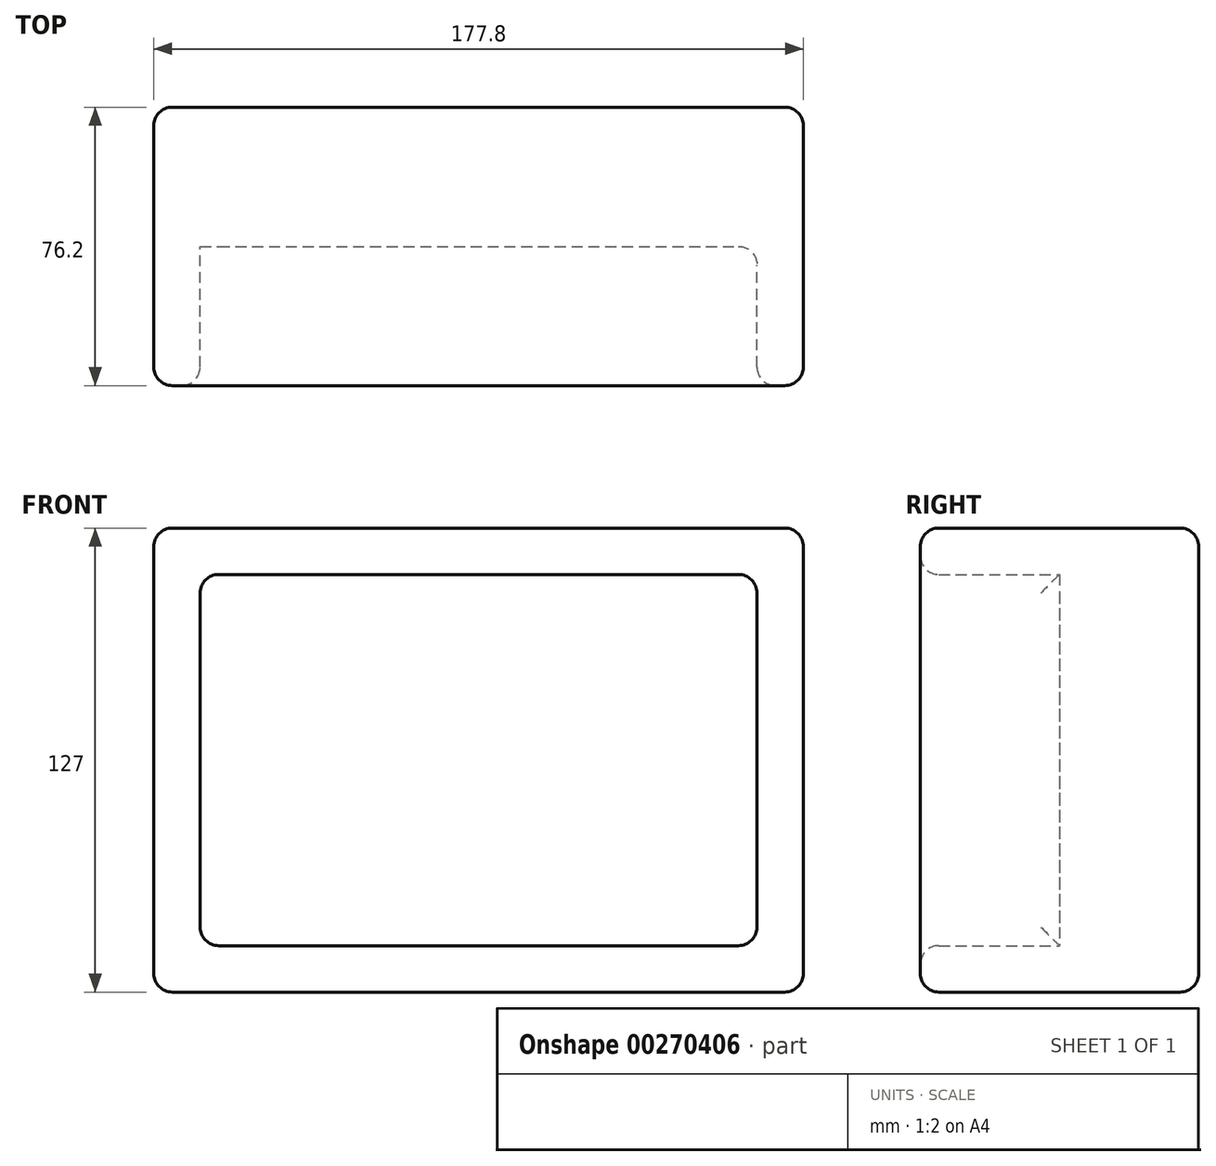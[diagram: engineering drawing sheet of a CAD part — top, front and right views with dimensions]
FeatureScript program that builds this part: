
annotation { "Feature Type Name" : "Feature", "Feature Type Description" : "" }
export const myFeature = defineFeature(function(context is Context, id is Id, definition is map)
    precondition{}
    {
        {
            var Q0;
            Q0=qCreatedBy(makeId("Front.planeOp"),FACE);
            var sketch = newSketch(context, id + "F0", { "sketchPlane" : qUnion([Q0])});
            skLineSegment(sketch, "E0.bottom", {"start": v(-88.9, 63.5) * mm, "end": v(88.9, 63.5) * mm});
            skLineSegment(sketch, "E0.top", {"start": v(-88.9, -63.5) * mm, "end": v(88.9, -63.5) * mm});
            skLineSegment(sketch, "E0.left", {"start": v(-88.9, 63.5) * mm, "end": v(-88.9, -63.5) * mm});
            skLineSegment(sketch, "E0.right", {"start": v(88.9, 63.5) * mm, "end": v(88.9, -63.5) * mm});
            skPoint(sketch, "E0.middle", {"position": v(0, 0) * mm});
            skLineSegment(sketch, "E1.bottom", {"start": v(-76.2, 50.8) * mm, "end": v(76.2, 50.8) * mm});
            skLineSegment(sketch, "E1.top", {"start": v(-76.2, -50.8) * mm, "end": v(76.2, -50.8) * mm});
            skLineSegment(sketch, "E1.left", {"start": v(-76.2, 50.8) * mm, "end": v(-76.2, -50.8) * mm});
            skLineSegment(sketch, "E1.right", {"start": v(76.2, 50.8) * mm, "end": v(76.2, -50.8) * mm});
            skSolve(sketch);
        }
        {
            var Q0;
            Q0=makeQuery(id+"F0.imprint","IMPRINT",FACE,{"disambiguationData":[TD([[makeQuery(id+"F0.imprint","IMPRINT",EDGE,{"derivedFrom":sQuery(id+"F0.wireOp",EDGE,"E0.bottom")}),-1.0]])]});
            extrude(context, id + "F1", {"entities" : qUnion([Q0]), "depth" : 76.2 * mm});
        }
        {
            var Q0;
            Q0=makeQuery(id+"F0.imprint","IMPRINT",FACE,{"disambiguationData":[TD([[makeQuery(id+"F0.imprint","IMPRINT",EDGE,{"derivedFrom":sQuery(id+"F0.wireOp",EDGE,"E1.bottom")}),-1.0]])]});
            extrude(context, id + "F2", {"entities" : qUnion([Q0]), "operationType" : NewBodyOperationType.ADD, "depth" : 38.1 * mm});
        }
        {
            var Q0;
            Q0=makeQuery(id+"F1.opExtrude","CAP_EDGE",EDGE,{"disambiguationData":[OSD([sQuery(id+"F0.wireOp",EDGE,"E0.left")])],"isStart":false});
            var Q1;
            Q1=makeQuery(id+"F1.opExtrude","CAP_FACE",FACE,{"disambiguationData":[OSD([sQuery(id+"F0.wireOp",EDGE,"E0.bottom"),sQuery(id+"F0.wireOp",EDGE,"E0.top"),sQuery(id+"F0.wireOp",EDGE,"E0.left"),sQuery(id+"F0.wireOp",EDGE,"E0.right"),sQuery(id+"F0.wireOp",EDGE,"E1.bottom"),sQuery(id+"F0.wireOp",EDGE,"E1.top"),sQuery(id+"F0.wireOp",EDGE,"E1.left"),sQuery(id+"F0.wireOp",EDGE,"E1.right")])],"isStart":false});
            var Q2;
            Q2=makeQuery(id+"F1.opExtrude","CAP_EDGE",EDGE,{"disambiguationData":[OSD([sQuery(id+"F0.wireOp",EDGE,"E0.bottom")])],"isStart":false});
            var Q3;
            Q3=makeQuery(id+"F1.opExtrude","CAP_EDGE",EDGE,{"disambiguationData":[OSD([sQuery(id+"F0.wireOp",EDGE,"E0.right")])],"isStart":false});
            var Q4;
            Q4=makeQuery(id+"F1.opExtrude","CAP_EDGE",EDGE,{"disambiguationData":[OSD([sQuery(id+"F0.wireOp",EDGE,"E0.top")])],"isStart":false});
            var Q5;
            Q5=makeQuery(id+"F1.opExtrude","CAP_EDGE",EDGE,{"disambiguationData":[OSD([sQuery(id+"F0.wireOp",EDGE,"E1.top")])],"isStart":false});
            var Q6;
            Q6=makeQuery(id+"F1.opExtrude","CAP_EDGE",EDGE,{"disambiguationData":[OSD([sQuery(id+"F0.wireOp",EDGE,"E1.left")])],"isStart":false});
            var Q7;
            Q7=makeQuery(id+"F2.opExtrude","CAP_EDGE",EDGE,{"disambiguationData":[OSD([sQuery(id+"F0.wireOp",EDGE,"E1.bottom")])],"isStart":false});
            var Q8;
            Q8=makeQuery(id+"F1.opExtrude","SWEPT_EDGE",EDGE,{"disambiguationData":[OSD([sQuery(id+"F0.wireOp",EDGE,"E1.bottom"),sQuery(id+"F0.wireOp",EDGE,"E1.right")])]});
            var Q9;
            Q9=makeQuery(id+"F2.opExtrude","CAP_EDGE",EDGE,{"disambiguationData":[OSD([sQuery(id+"F0.wireOp",EDGE,"E1.right")])],"isStart":false});
            var Q10;
            Q10=makeQuery(id+"F1.opExtrude","SWEPT_FACE",FACE,{"disambiguationData":[OSD([sQuery(id+"F0.wireOp",EDGE,"E1.right")])]});
            var Q11;
            Q11=makeQuery(id+"F2.opExtrude","CAP_EDGE",EDGE,{"disambiguationData":[OSD([sQuery(id+"F0.wireOp",EDGE,"E1.top")])],"isStart":false});
            var Q12;
            Q12=makeQuery(id+"F1.opExtrude","SWEPT_EDGE",EDGE,{"disambiguationData":[OSD([sQuery(id+"F0.wireOp",EDGE,"E1.bottom"),sQuery(id+"F0.wireOp",EDGE,"E1.left")])]});
            var Q13;
            Q13=makeQuery(id+"F2.opExtrude","CAP_EDGE",EDGE,{"disambiguationData":[OSD([sQuery(id+"F0.wireOp",EDGE,"E1.left")])],"isStart":false});
            var Q14;
            Q14=makeQuery(id+"F1.opExtrude","SWEPT_EDGE",EDGE,{"disambiguationData":[OSD([sQuery(id+"F0.wireOp",EDGE,"E1.top"),sQuery(id+"F0.wireOp",EDGE,"E1.left")])]});
            var Q15;
            Q15=makeQuery(id+"F1.opExtrude","SWEPT_EDGE",EDGE,{"disambiguationData":[OSD([sQuery(id+"F0.wireOp",EDGE,"E0.bottom"),sQuery(id+"F0.wireOp",EDGE,"E0.left")])]});
            var Q16;
            Q16=makeQuery(id+"F1.opExtrude","CAP_EDGE",EDGE,{"disambiguationData":[OSD([sQuery(id+"F0.wireOp",EDGE,"E0.top")])],"isStart":true});
            var Q17;
            Q17=makeQuery(id+"F1.opExtrude","CAP_EDGE",EDGE,{"disambiguationData":[OSD([sQuery(id+"F0.wireOp",EDGE,"E0.left")])],"isStart":true});
            var Q18;
            Q18=makeQuery(id+"F1.opExtrude","SWEPT_EDGE",EDGE,{"disambiguationData":[OSD([sQuery(id+"F0.wireOp",EDGE,"E0.top"),sQuery(id+"F0.wireOp",EDGE,"E0.left")])]});
            var Q19;
            Q19=makeQuery(id+"F1.opExtrude","SWEPT_FACE",FACE,{"disambiguationData":[OSD([sQuery(id+"F0.wireOp",EDGE,"E0.right")])]});
            var Q20;
            Q20=makeQuery(id+"F1.opExtrude","CAP_EDGE",EDGE,{"disambiguationData":[OSD([sQuery(id+"F0.wireOp",EDGE,"E0.right")])],"isStart":true});
            var Q21;
            {var subQ0=sQuery(id+"F0.wireOp",EDGE,"E1.right");var subQ1=sQuery(id+"F0.wireOp",EDGE,"E1.left");var subQ2=sQuery(id+"F0.wireOp",EDGE,"E1.top");var subQ3=sQuery(id+"F0.wireOp",EDGE,"E1.bottom");Q21=makeQuery(id+"F2.boolean.opBoolean","MERGE",FACE,{"derivedFrom":[makeQuery(id+"F1.opExtrude","CAP_FACE",FACE,{"disambiguationData":[OSD([sQuery(id+"F0.wireOp",EDGE,"E0.bottom"),sQuery(id+"F0.wireOp",EDGE,"E0.top"),sQuery(id+"F0.wireOp",EDGE,"E0.left"),sQuery(id+"F0.wireOp",EDGE,"E0.right"),subQ3,subQ2,subQ1,subQ0])],"isStart":true}),makeQuery(id+"F2.opExtrude","CAP_FACE",FACE,{"disambiguationData":[OSD([subQ3,subQ2,subQ1,subQ0])],"isStart":true})]});}
            fillet(context, id + "F3", {"entities" : qUnion([Q0, Q1, Q2, Q3, Q4, Q5, Q6, Q7, Q8, Q9, Q10, Q11, Q12, Q13, Q14, Q15, Q16, Q17, Q18, Q19, Q20, Q21]), "radius" : 5.08 * mm, "tangentPropagation" : true, "allowEdgeOverflow" : false});
        }
    });
